# Revit family: Haworth_BuzziMe_LoungeChair_AP_PRELIMINARY
name_source: partatom
category: Furniture
revit_build: Autodesk Revit 2018 (Build: 20170223_1515(x64)
units: mm (PartAtom-declared; Revit-internal decimal feet)

## family parameters
Always vertical = Yes
Cut with Voids When Loaded = No
OmniClass Number = 23.40.20.00
OmniClass Title = General Furniture and Specialties
Room Calculation Point = No
Shared = No
Work Plane-Based = No

## types (4) — shared parameters
Actual Depth = 935 mm
Actual Width = 715 mm
Assembly Code = E2020200
Description = Haworth - BuzziMe - Lounge Chair
Manufacturer = Haworth
Model = BuzziMe
Revision = 1
Size = Verify Final Dim. w/ Haworth
Tablet Finish = Haworth _ Paint _ Umbra Grey
URL = https://www.haworth.com
URL - Product = https://www.haworth.com
Warranty = http://www.haworth.com

## per-type parameters (varying)
| type | Actual Height | Headrest | Tablet |
| With Headrest - With Tablet | 1350 mm | Yes | Yes |
| Without Headrest - With Tablet | 950 mm | No | Yes |
| With Headrest - Without Tablet | 1350 mm | Yes | No |
| Without Headrest - Without Tablet | 950 mm | No | No |

## geometry (parser evidence)
native form markers: Sweep x3
no freeform markers — native parametric forms only
